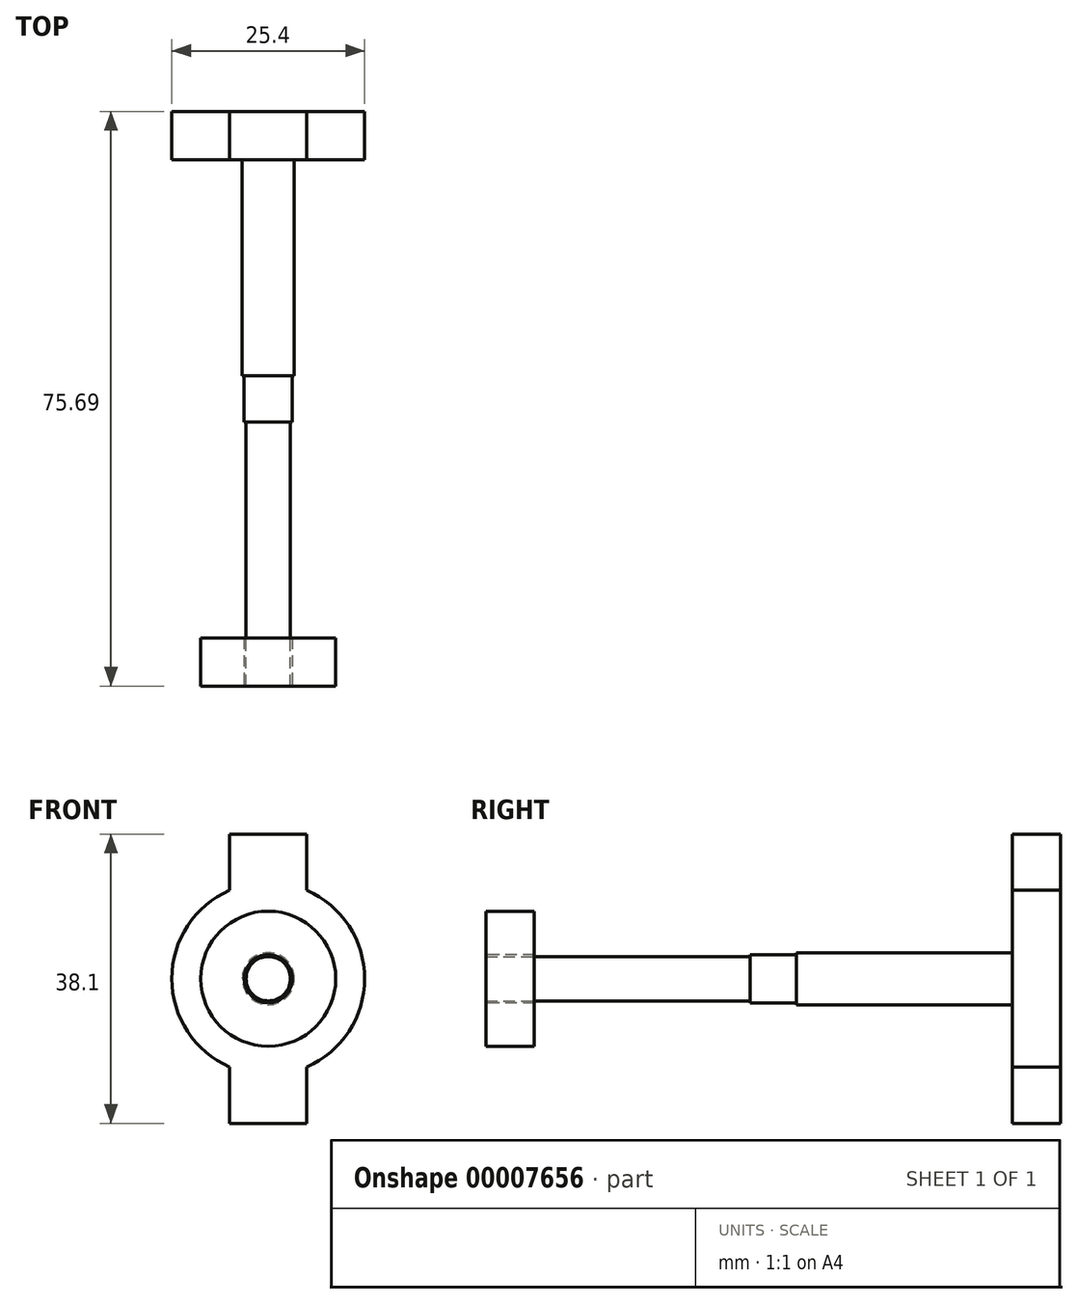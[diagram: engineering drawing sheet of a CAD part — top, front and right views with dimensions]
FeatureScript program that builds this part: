
annotation { "Feature Type Name" : "Feature", "Feature Type Description" : "" }
export const myFeature = defineFeature(function(context is Context, id is Id, definition is map)
    precondition{}
    {
        {
            var Q0;
            Q0=qCreatedBy(makeId("Front.planeOp"),FACE);
            var sketch = newSketch(context, id + "F0", { "sketchPlane" : qUnion([Q0])});
            skCircle(sketch, "E0", {"center": v(0, 0) * mm, "radius": 3.43 * mm});
            skSolve(sketch);
        }
        {
            var Q0;
            Q0 = qSketchRegion(id + "F0", true);
            extrude(context, id + "F1", {"entities" : qUnion([Q0]), "depth" : 28.45 * mm});
        }
        {
            var Q0;
            Q0=makeQuery(id+"F1.opExtrude","CAP_FACE",FACE,{"disambiguationData":[OSD([sQuery(id+"F0.wireOp",EDGE,"E0")])],"isStart":false});
            var sketch = newSketch(context, id + "F2", { "sketchPlane" : qUnion([Q0])});
            skCircle(sketch, "E1", {"center": v(0, 0) * mm, "radius": 3.18 * mm});
            skSolve(sketch);
        }
        {
            var Q0;
            Q0 = qSketchRegion(id + "F2", true);
            extrude(context, id + "F3", {"entities" : qUnion([Q0]), "operationType" : NewBodyOperationType.ADD, "depth" : 6.1 * mm});
        }
        {
            var Q0;
            Q0=makeQuery(id+"F3.opExtrude","CAP_FACE",FACE,{"disambiguationData":[OSD([sQuery(id+"F2.wireOp",EDGE,"E1")])],"isStart":false});
            var sketch = newSketch(context, id + "F4", { "sketchPlane" : qUnion([Q0])});
            skCircle(sketch, "E2", {"center": v(0, 0) * mm, "radius": 2.92 * mm});
            skSolve(sketch);
        }
        {
            var Q0;
            Q0 = qSketchRegion(id + "F4", true);
            extrude(context, id + "F5", {"entities" : qUnion([Q0]), "operationType" : NewBodyOperationType.ADD, "depth" : 34.8 * mm});
        }
        {
            var Q0;
            Q0=makeQuery(id+"F1.opExtrude","CAP_FACE",FACE,{"disambiguationData":[OSD([sQuery(id+"F0.wireOp",EDGE,"E0")])],"isStart":true});
            var sketch = newSketch(context, id + "F6", { "sketchPlane" : qUnion([Q0])});
            skCircle(sketch, "E3", {"center": v(0, 0) * mm, "radius": 12.7 * mm});
            skSolve(sketch);
        }
        {
            var Q0;
            Q0 = qSketchRegion(id + "F6", true);
            extrude(context, id + "F7", {"entities" : qUnion([Q0]), "operationType" : NewBodyOperationType.ADD, "depth" : 6.35 * mm});
        }
        {
            var Q0;
            Q0=makeQuery(id+"F5.opExtrude","CAP_FACE",FACE,{"disambiguationData":[OSD([sQuery(id+"F4.wireOp",EDGE,"E2")])],"isStart":false});
            var sketch = newSketch(context, id + "F8", { "sketchPlane" : qUnion([Q0])});
            skCircle(sketch, "E4", {"center": v(0, 0) * mm, "radius": 8.9 * mm});
            skCircle(sketch, "E5", {"center": v(0, 0) * mm, "radius": 3.18 * mm});
            skSolve(sketch);
        }
        {
            var Q0;
            Q0 = qSketchRegion(id + "F8", true);
            extrude(context, id + "F9", {"entities" : qUnion([Q0]), "operationType" : NewBodyOperationType.ADD, "oppositeDirection" : true, "depth" : 6.35 * mm});
        }
        {
            var Q0;
            Q0=qCreatedBy(makeId("Top.planeOp"),FACE);
            var sketch = newSketch(context, id + "F10", { "sketchPlane" : qUnion([Q0])});
            skLineSegment(sketch, "E6.bottom", {"start": v(-5.08, 0) * mm, "end": v(5.08, 0) * mm});
            skLineSegment(sketch, "E6.top", {"start": v(-5.08, 6.35) * mm, "end": v(5.08, 6.35) * mm});
            skLineSegment(sketch, "E6.left", {"start": v(-5.08, 0) * mm, "end": v(-5.08, 6.35) * mm});
            skLineSegment(sketch, "E6.right", {"start": v(5.08, 0) * mm, "end": v(5.08, 6.35) * mm});
            skSolve(sketch);
        }
        {
            var Q0;
            Q0 = qSketchRegion(id + "F10", true);
            extrude(context, id + "F11", {"entities" : qUnion([Q0]), "operationType" : NewBodyOperationType.ADD, "endBound" : BoundingType.SYMMETRIC, "depth" : 38.1 * mm});
        }
    });
